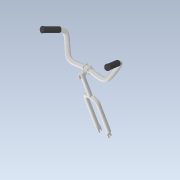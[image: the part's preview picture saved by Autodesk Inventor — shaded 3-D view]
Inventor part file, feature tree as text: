
AUTODESK INVENTOR PART (.ipt)
format: ipt  version: 2021 (Build 250183000, 183)  size: 5,145,600 bytes
history: native  units: in
note: dims shown in document units (in); Inventor stores cm internally (conversion verified against a paired STEP export)
features: plane x34, sketch x28, other x15, extrude x14, projected_geometry x9, loft x5, fillet x4, mirror x4, hole x2, split x2, sweep x1, move_body x1, chamfer x1, revolve x1
ambient origin geometry x8: Origin, YZ Plane, XZ Plane, XY Plane, X Axis, Y Axis, Z Axis, Center Point
bodies: Solid4 (feature_tree)
feature tree (121):
  sketch  "3D Sketch1"
  plane  "Work Plane6"
  sweep  "Sweep3"
  plane  "Work Plane4"
  plane  "Work Plane5"
  sketch  "Sketch14"  dims[d24=1.66in d25=0.0in d26=0.0in]
  sketch  "Sketch15"  dims[d28=2.0472in d29=0.0in d30=90.0deg d31=0.0in d32=90.0deg]
  loft  "Loft1"
  loft  "Loft2"
  plane  "Work Plane7"
  sketch  "Sketch16"  dims[d33=0.0in d34=90.0deg d35=0.0in d36=90.0deg d37=0.0in d42=180.0deg]
  plane  "Work Plane8"
  extrude  "Extrusion2"  TaperAngle=180.0deg  [1 undecoded]
  extrude  "Extrusion3"  Depth=1.378in TaperAngle=0.0deg
  plane  "Work Plane9"
  extrude  "Extrusion4"  Depth=1.7225in TaperAngle=0.0deg
  extrude  "Extrusion5"  Depth=1.1024in
  plane  "Work Plane22"
  sketch  "Sketch33"  dims[d112=0.3937in d113=0.0in d114=0.3937in d115=0.0in]
  plane  "Work Plane23"
  extrude  "Extrusion10"  Depth=0.1969in
  plane  "Work Plane19"
  plane  "Work Plane20"
  extrude  "Extrusion11"  Depth=0.4331in
  fillet  "Fillet1"  Radius=0.0197in
  plane  "Work Plane24"
  plane  "Work Plane25"
  hole  "Hole1"  [1 undecoded]
  mirror  "Mirror5"
  other  "Work Axis4"
  mirror  "Mirror3"
  plane  "Work Plane34"
  extrude  "Extrusion13"  Depth=0.3937in TaperAngle=0.0deg
  fillet  "Fillet2"  Radius=0.0984in
  plane  "Work Plane35"
  hole  "Hole2"  [1 undecoded]
  plane  "Work Plane36"
  sketch  "Sketch44"  dims[d149=1.1024in]
  split  "Split2"
  plane  "Work Plane26"
  split  "Split1"
  other  "Work Axis1"
  move_body  "Move Body2"
  plane  "Work Plane10"
  plane  "Work Plane11"
  plane  "Work Plane12"
  extrude  "Extrusion6"  [1 undecoded]
  sketch  "Sketch23"  dims[d73=0.3937in d74=0.0in d79=0.4331in d80=0.0197in]
  loft  "Loft5"
  loft  "Loft8"
  plane  "Work Plane13"
  extrude  "Extrusion8"  TaperAngle=180.0deg  [1 undecoded]
  other  "Work Axis5"
  other  "Bend Part2"
  plane  "Work Plane30"
  sketch  "Sketch36"  dims[d121=2.0in d122=0.1575in d123=0.0787in d124=90.0deg d125=1.66in d126=0.8108in]
  loft  "Loft10"
  plane  "Work Plane41"
  plane  "Work Plane31"
  extrude  "Extrusion17"  TaperAngle=90.0deg  [1 undecoded]
  plane  "Work Plane32"
  extrude  "Extrusion12"  Depth=1.38in
  chamfer  "Chamfer1"  Distance=0.7874in
  fillet  "Fillet4"  Radius=1.9685in
  mirror  "Mirror6"
  plane  "Work Plane33"
  sketch  "Sketch41"  dims[d138=1.38in d139=1.66in]
  plane  "Work Plane37"
  revolve  "Revolution2"  [1 undecoded]
  plane  "Work Plane38"
  extrude  "Extrusion14"  TaperAngle=0.0deg  [1 undecoded]
  plane  "Work Plane39"
  extrude  "Extrusion15"  Depth=0.1969in
  fillet  "Fillet3"  Radius=0.3937in
  plane  "Work Plane40"
  extrude  "Extrusion16"  Depth=0.4921in
  mirror  "Mirror7"
  sketch  "Sketch13"  dims[d19=0.0in d21=1.378in d23=1.38in]
  other  "Caña Dirección"
  sketch  "Sketch17"  dims[d43=0.3937in d44=0.0in d45=1.378in d46=0.0in]
  sketch  "Sketch18"  dims[d48=180.0deg d49=1.7225in d50=0.0in]
  sketch  "Sketch19"  dims[d53=0.8661in d54=0.0in d55=1.1024in]
  sketch  "Sketch20"  dims[d57=180.0deg d60=0.1969in]
  other  "Tubo Tenedor Central"
  sketch  "Sketch25"  dims[d85=14.9449in d86=1.38in]
  other  "Tubo Tenedor Der"
  plane  "Work Plane18"
  sketch  "Sketch32"  dims[d94=0.0in d95=90.0deg d96=0.0in d97=90.0deg d98=0.3937in d99=0.0in d105=0.0984in]
  plane  "Work Plane21"
  sketch  "Sketch34"  dims[d116=0.1969in d117=-1.0236in]
  plane  "Work Plane27"
  plane  "Work Plane28"
  sketch  "Sketch35"  dims[d119=0.1181in]
  other  "Pattern of Tubo Tenedor Der:2"
  other  "Tubo Tenedor Izq"
  plane  "Work Plane29"
  sketch  "Sketch37"  dims[d127=0.4921in d128=0.0in]
  sketch  "Sketch40"  dims[d131=90.0deg d132=180.0deg]
  sketch  "Sketch42"  dims[d140=1.66in d144=90.0deg]
  sketch  "Sketch43"  dims[d145=180.0deg d146=1.38in]
  sketch  "Sketch45"  dims[d152=1.0817in]
  other  "Copa Tenedor"
  sketch  "Sketch46"  dims[d153=90.0deg d154=0.0in d155=0.7874in d180=1.9685in]
  other  "Mango Izq"
  sketch  "Sketch47"  dims[d193=0.1969in d196=0.0in d197=0.0in]
  sketch  "Sketch48"  dims[d198=0.0in d205=0.0in]
  other  "Pattern of Mango Izq:3"
  other  "Mango Der"
  sketch  "Sketch49"  dims[d206=0.9843in d208=0.7874in d210=0.1969in d211=0.3937in d212=0.0in]
  sketch  "Sketch50"  dims[d215=0.3369in d216=0.4921in d218=0.5629in d219=0.2362in d220=0.1181in d221=0.0in d222=0.1969in d223=0.2362in d224=0.1575in d225=0.0787in d226=90.0deg d227=1.66in d228=0.8108in d229=0.0in d236=0.0in d237=90.0deg d238=0.0in d239=90.0deg d246=0.14in d247=0.315in d248=0.83in d249=90.0deg d250=-3.937in d251=1.9685in d252=5.9055in d253=0.0in d254=0.0in d255=2.1654in d256=0.3937in d257=0.0in d258=0.0787in d259=0.0in d260=0.1575in d261=0.3937in d262=0.0in d265=0.0in d266=90.0deg d269=0.3937in d270=0.0in d271=90.0deg d272=0.0in d273=0.3937in d274=0.0in d275=0.69in d276=0.7815in d277=0.1969in d278=0.0787in d279=45.0deg d280=0.0787in d141=0.0344in]
  projected_geometry  "Project Cut Edges2"
  projected_geometry  "Project Cut Edges3"
  projected_geometry  "Project Cut Edges4"
  projected_geometry  "Project Cut Edges5"
  projected_geometry  "Project Cut Edges6"
  projected_geometry  "Project Cut Edges7"
  other  "Potencia Del"
  other  "Potencia Tras"
  projected_geometry  "Project Cut Edges10"
  projected_geometry  "Project Cut Edges11"
  projected_geometry  "Project Cut Edges12"
note: 8 required parameter values undecoded (feature->parameter linkage not recoverable at this tier; creation-order binding heuristic only, values carry confidence <= 0.55)